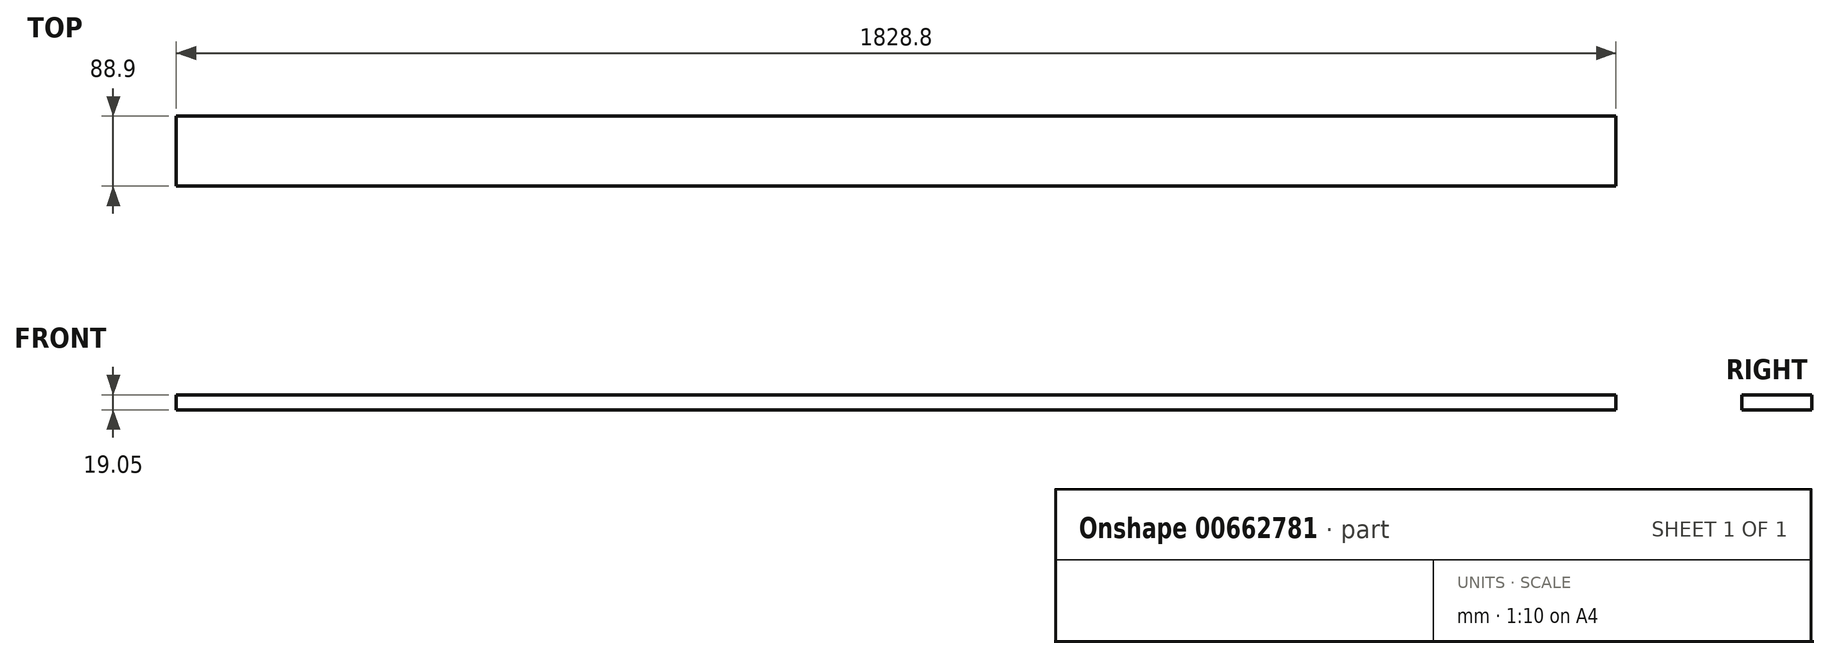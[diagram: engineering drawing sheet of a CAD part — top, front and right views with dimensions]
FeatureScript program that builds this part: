
annotation { "Feature Type Name" : "Feature", "Feature Type Description" : "" }
export const myFeature = defineFeature(function(context is Context, id is Id, definition is map)
    precondition{}
    {
        {
            var Q0;
            Q0=qCreatedBy(makeId("Top.planeOp"),FACE);
            var sketch = newSketch(context, id + "F0", { "sketchPlane" : qUnion([Q0])});
            skLineSegment(sketch, "E0.bottom", {"start": v(-914.4, 44.45) * mm, "end": v(914.4, 44.45) * mm});
            skLineSegment(sketch, "E0.top", {"start": v(-914.4, -44.45) * mm, "end": v(914.4, -44.45) * mm});
            skLineSegment(sketch, "E0.left", {"start": v(-914.4, 44.45) * mm, "end": v(-914.4, -44.45) * mm});
            skLineSegment(sketch, "E0.right", {"start": v(914.4, 44.45) * mm, "end": v(914.4, -44.45) * mm});
            skPoint(sketch, "E0.middle", {"position": v(0, 0) * mm});
            skSolve(sketch);
        }
        {
            var Q0;
            Q0=makeQuery(id+"F0.imprint","IMPRINT",FACE,{"disambiguationData":[TD([[makeQuery(id+"F0.imprint","IMPRINT",EDGE,{"derivedFrom":sQuery(id+"F0.wireOp",EDGE,"E0.bottom")}),-1.0]])]});
            extrude(context, id + "F1", {"entities" : qUnion([Q0]), "depth" : 19.05 * mm, "offsetDistance" : 25.4 * mm});
        }
    });
